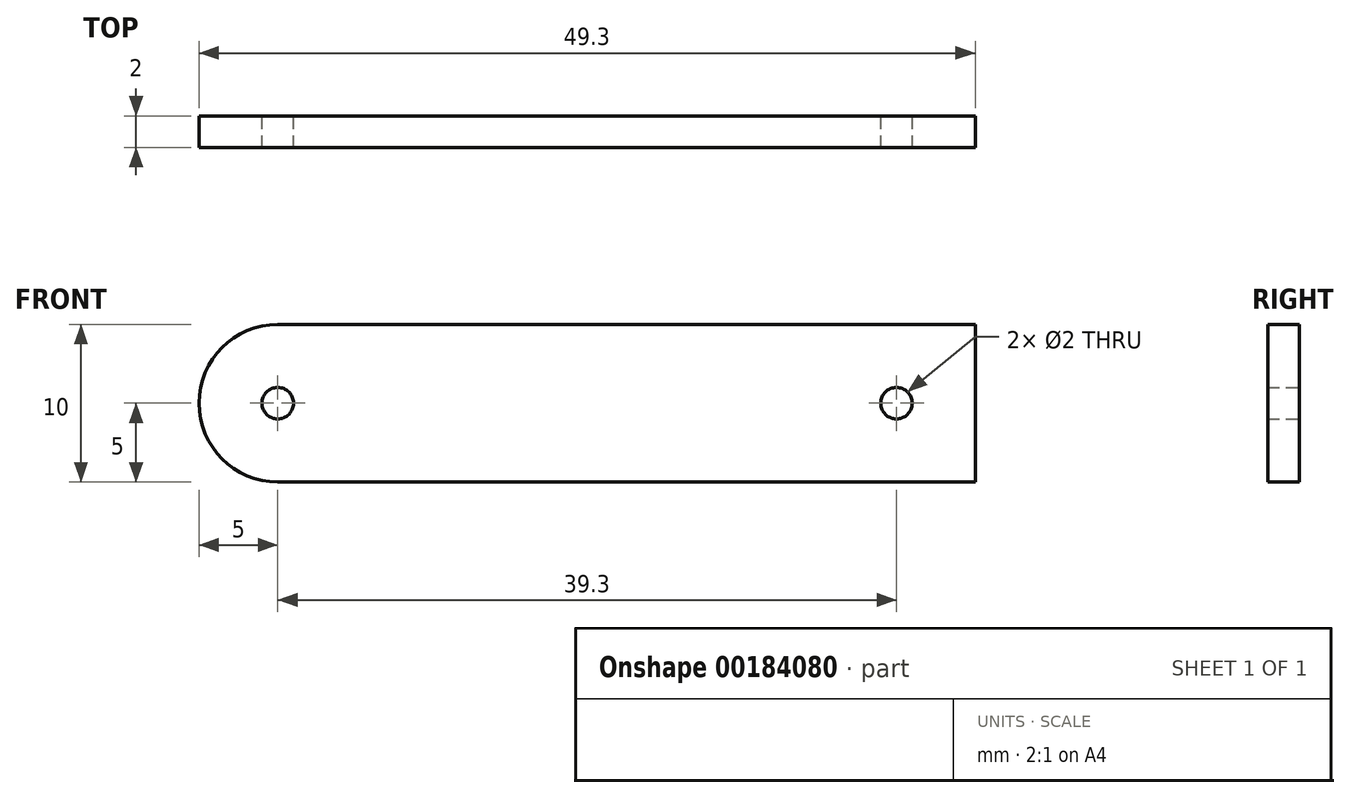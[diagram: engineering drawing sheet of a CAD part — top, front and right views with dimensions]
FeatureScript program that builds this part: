
annotation { "Feature Type Name" : "Feature", "Feature Type Description" : "" }
export const myFeature = defineFeature(function(context is Context, id is Id, definition is map)
    precondition{}
    {
        {
            var Q0;
            Q0=qCreatedBy(makeId("Front.planeOp"),FACE);
            var sketch = newSketch(context, id + "F0", { "sketchPlane" : qUnion([Q0])});
            skLineSegment(sketch, "E0.bottom", {"start": v(0, 0) * mm, "end": v(44.3, 0) * mm});
            skLineSegment(sketch, "E0.top", {"start": v(0, -10) * mm, "end": v(44.3, -10) * mm});
            skLineSegment(sketch, "E0.right", {"start": v(44.3, 0) * mm, "end": v(44.3, -10) * mm});
            skArc(sketch, "E1", {"start": v(0, 0) * mm, "mid": v(-5, -5) * mm, "end": v(0, -10) * mm});
            skCircle(sketch, "E2", {"center": v(0, -5) * mm, "radius": 1 * mm});
            skCircle(sketch, "E3", {"center": v(39.3, -5) * mm, "radius": 1 * mm});
            skSolve(sketch);
        }
        {
            var Q0;
            Q0=makeQuery(id+"F0.imprint","IMPRINT",FACE,{"disambiguationData":[TD([[makeQuery(id+"F0.imprint","IMPRINT",EDGE,{"derivedFrom":sQuery(id+"F0.wireOp",EDGE,"E0.bottom")}),-1.0]])]});
            extrude(context, id + "F1", {"entities" : qUnion([Q0]), "depth" : 2 * mm});
        }
    });
